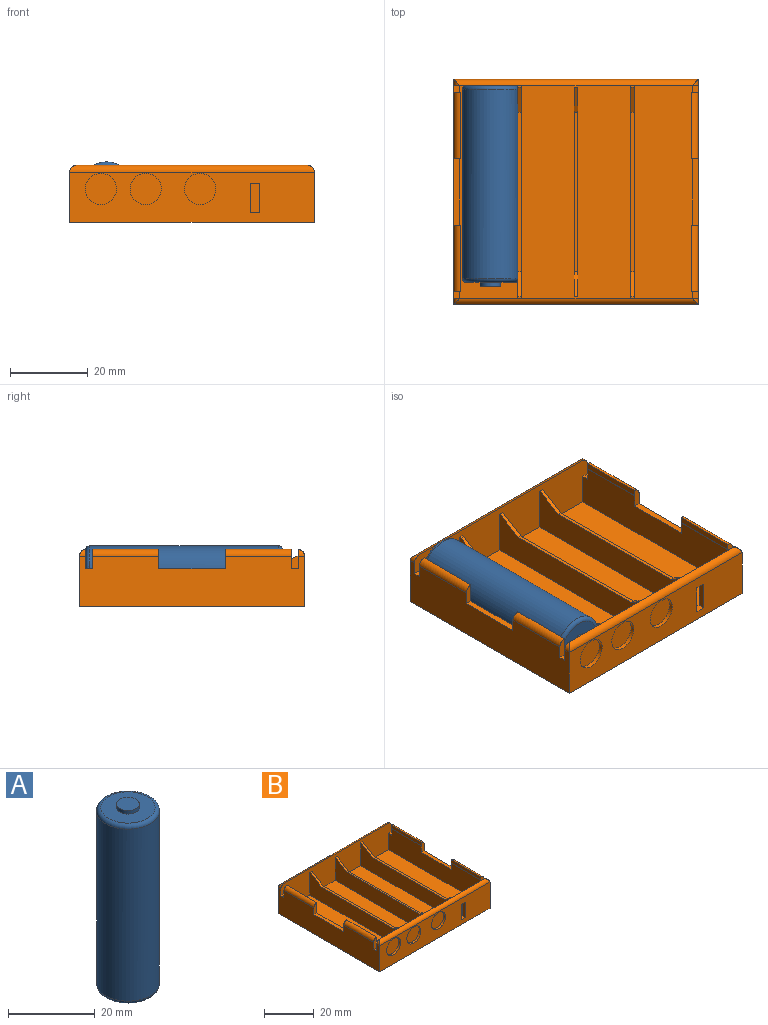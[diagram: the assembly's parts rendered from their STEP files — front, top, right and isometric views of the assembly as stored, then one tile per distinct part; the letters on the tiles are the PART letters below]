
ASSEMBLY  parts=2 mates=1
PART A: 7 faces, bbox 15.7x15.7x51.5 mm
  f0: plane 12.5x12.5mm, normal (0,0,-1), area 122.7mm2, adj f5
  f1: cylinder r=7.25mm len=48.5mm, axis (0,0,-1), area 2209.3mm2, adj f5,f6
  f2: plane 12.5x12.5mm, normal (0,0,1), area 101mm2, adj f3,f6
  f3: cylinder r=2.63mm len=5.26mm, axis (0,0,-1), area 16.5mm2, adj f2,f4
  f4: plane 5.26x5.26mm, normal (0,0,1), area 21.7mm2, adj f3
  f5: torus R=6.25mm, axis (0,0,1), area 68mm2, adj f0,f1
  f6: torus R=6.25mm, axis (0,0,-1), area 68mm2, adj f1,f2
PART B: 81 faces, bbox 62.8x57.8x14.6 mm
  f0: plane 54.6x14.8mm, normal (0,0,1), area 808.1mm2, adj f1,f4,f29,f74
  f1: plane 62.81x13.01mm, normal (0,-1,0), area 755.7mm2, adj f0,f2,f3,f7,f8,f12,f19,f24
  f2: plane 54.6x13.5mm, normal (0,0,1), area 737.1mm2, adj f1,f4,f68,f75
  f3: plane 54.6x13.5mm, normal (0,0,1), area 737.1mm2, adj f1,f4,f60,f67
  f4: plane 62.81x13.01mm, normal (0,1,0), area 737.7mm2, adj f0,f2,f3,f5,f6,f7,f10,f11
  f5: plane 2.4x1.6mm, normal (0,0,1), area 3.8mm2, adj f4,f21,f59,f61
  f6: plane 2.4x1.6mm, normal (0,0,-1), area 3.8mm2, adj f4,f21,f59,f61
  f7: plane 57.8x12.85mm, normal (-1,0,0), area 675.8mm2, adj f1,f4,f12,f13,f14,f20,f21,f22
  f8: cylinder r=1.75mm len=1.74mm, axis (0,-1,0), area 2.1mm2, adj f1,f19,f24
  f9: cylinder r=1.75mm len=17mm, axis (0,-1,0), area 46.7mm2, adj f15,f19,f41,f45
  f10: cylinder r=1.75mm len=1.74mm, axis (0,-1,0), area 2.1mm2, adj f4,f11,f19
  f11: cylinder r=1.75mm len=62.8mm, axis (-1,0,0), area 159.1mm2, adj f4,f10,f14,f21
  f12: cylinder r=1.75mm len=1.74mm, axis (0,1,0), area 2.1mm2, adj f1,f7,f24
  f13: cylinder r=1.75mm len=17mm, axis (0,1,0), area 46.7mm2, adj f7,f16,f37,f42
  f14: cylinder r=1.75mm len=1.74mm, axis (0,1,0), area 2.1mm2, adj f4,f7,f11
  f15: plane 17x1.6mm, normal (-1,0,0), area 27.2mm2, adj f9,f17,f41,f45
  f16: plane 17x1.6mm, normal (1,0,0), area 27.2mm2, adj f13,f18,f37,f42
  f17: cylinder r=0.15mm len=17mm, axis (0,-1,0), area 4mm2, adj f15,f28,f41,f45
  f18: cylinder r=0.15mm len=17mm, axis (0,1,0), area 4mm2, adj f16,f29,f37,f42
  f19: plane 57.8x12.85mm, normal (1,0,0), area 675.8mm2, adj f1,f4,f8,f9,f10,f20,f21,f22
  f20: plane 62.8x12.85mm, normal (0,1,0), area 676.8mm2, adj f7,f19,f22,f24,f47,f49,f51
  f21: plane 62.8x12.85mm, normal (0,-1,0), area 638.2mm2, adj f5,f6,f7,f11,f19,f22,f53,f54
  f22: plane 62.8x57.8mm, normal (0,0,-1), area 3629.8mm2, adj f7,f19,f20,f21
  f23: cylinder r=1.75mm len=17mm, axis (0,-1,0), area 46.7mm2, adj f19,f26,f34,f46
  f24: cylinder r=1.75mm len=62.8mm, axis (1,0,0), area 159.1mm2, adj f1,f8,f12,f20
  f25: cylinder r=1.75mm len=17mm, axis (0,1,0), area 46.7mm2, adj f7,f27,f35,f38
  f26: plane 17x1.6mm, normal (-1,0,0), area 27.2mm2, adj f23,f31,f34,f46
  f27: plane 17x1.6mm, normal (1,0,0), area 27.2mm2, adj f25,f32,f35,f38
  f28: plane 54.6x11.25mm, normal (-1,0,0), area 547.3mm2, adj f1,f4,f17,f30,f31,f33,f34,f40
  f29: plane 54.6x11.25mm, normal (1,0,0), area 547.3mm2, adj f0,f1,f4,f18,f32,f35,f36,f37
  f30: plane 54.6x14.8mm, normal (0,0,1), area 808.1mm2, adj f1,f4,f28,f61
  f31: cylinder r=0.15mm len=17mm, axis (0,-1,0), area 4mm2, adj f26,f28,f34,f46
  f32: cylinder r=0.15mm len=17mm, axis (0,1,0), area 4mm2, adj f27,f29,f35,f38
  f33: plane 1.8x1.6mm, normal (0,0,1), area 2.9mm2, adj f4,f19,f28,f34
  f34: plane 5x1.75mm, normal (0,-1,0), area 7.6mm2, adj f19,f23,f26,f28,f31,f33
  f35: plane 5x1.75mm, normal (0,-1,0), area 7.6mm2, adj f7,f25,f27,f29,f32,f36
  f36: plane 1.8x1.6mm, normal (0,0,1), area 2.9mm2, adj f4,f7,f29,f35
  f37: plane 5x1.75mm, normal (0,-1,0), area 7.6mm2, adj f7,f13,f16,f18,f29,f39
  f38: plane 5x1.75mm, normal (0,1,0), area 7.6mm2, adj f7,f25,f27,f29,f32,f39
  f39: plane 17x1.6mm, normal (0,0,1), area 27.2mm2, adj f7,f29,f37,f38
  f40: plane 1.8x1.6mm, normal (0,0,1), area 2.9mm2, adj f1,f19,f28,f41
  f41: plane 5x1.75mm, normal (0,1,0), area 7.6mm2, adj f9,f15,f17,f19,f28,f40
  f42: plane 5x1.75mm, normal (0,1,0), area 7.6mm2, adj f7,f13,f16,f18,f29,f43
  f43: plane 1.8x1.6mm, normal (0,0,1), area 2.9mm2, adj f1,f7,f29,f42
  f44: plane 17x1.6mm, normal (0,0,1), area 27.2mm2, adj f19,f28,f45,f46
  f45: plane 5x1.75mm, normal (0,-1,0), area 7.6mm2, adj f9,f15,f17,f19,f28,f44
  f46: plane 5x1.75mm, normal (0,1,0), area 7.6mm2, adj f19,f23,f26,f28,f31,f44
  f47: cylinder r=3.65mm len=7.3mm, axis (0,1,0), area 11.5mm2, adj f20,f48
  f48: plane 7.3x7.3mm, normal (0,1,0), area 41.9mm2, adj f47
  f49: cylinder r=3.75mm len=7.5mm, axis (0,1,0), area 11.8mm2, adj f20,f50
  f50: plane 7.5x7.5mm, normal (0,1,0), area 44.2mm2, adj f49
  f51: cylinder r=3.75mm len=7.5mm, axis (0,1,0), area 11.8mm2, adj f20,f52
  f52: plane 7.5x7.5mm, normal (0,1,0), area 44.2mm2, adj f51
  f53: cylinder r=4mm len=8mm, axis (0,-1,0), area 25.1mm2, adj f21,f58
  f54: cylinder r=4mm len=8mm, axis (0,-1,0), area 25.1mm2, adj f21,f57
  f55: cylinder r=4mm len=8mm, axis (0,-1,0), area 25.1mm2, adj f21,f56
  f56: plane 8x8mm, normal (0,-1,0), area 50.3mm2, adj f55
  f57: plane 8x8mm, normal (0,-1,0), area 50.3mm2, adj f54
  f58: plane 8x8mm, normal (0,-1,0), area 50.3mm2, adj f53
  f59: plane 7.5x1.6mm, normal (-1,0,0), area 12mm2, adj f4,f5,f6,f21
  f60: plane 54.6x11.25mm, normal (-1,0,0), area 426.7mm2, adj f1,f3,f4,f62,f63,f64,f65,f66
  f61: plane 56.2x11.25mm, normal (1,0,0), area 438.7mm2, adj f1,f4,f5,f6,f21,f30,f62,f63
  f62: plane 1x0.4mm, normal (0,0,1), area 0.4mm2, adj f1,f60,f61,f63
  f63: plane 6.37x3.95mm, normal (0,-0.53,0.85), area 7.5mm2, adj f60,f61,f62,f64
  f64: plane 41.05x1mm, normal (0,0,1), area 41.1mm2, adj f60,f61,f63,f65
  f65: plane 6.37x3.95mm, normal (0,0.53,0.85), area 7.5mm2, adj f60,f61,f64,f66
  f66: plane 1x0.4mm, normal (0,0,1), area 0.4mm2, adj f4,f60,f61,f65
  f67: plane 54.6x11.25mm, normal (1,0,0), area 426.7mm2, adj f1,f3,f4,f69,f70,f71,f72,f73
  f68: plane 54.6x11.25mm, normal (-1,0,0), area 426.7mm2, adj f1,f2,f4,f69,f70,f71,f72,f73
  f69: plane 1x0.4mm, normal (0,0,1), area 0.4mm2, adj f4,f67,f68,f70
  f70: plane 6.37x3.95mm, normal (0,0.53,0.85), area 7.5mm2, adj f67,f68,f69,f71
  f71: plane 41.05x1mm, normal (0,0,1), area 41.1mm2, adj f67,f68,f70,f72
  f72: plane 6.37x3.95mm, normal (0,-0.53,0.85), area 7.5mm2, adj f67,f68,f71,f73
  f73: plane 1x0.4mm, normal (0,0,1), area 0.4mm2, adj f1,f67,f68,f72
  f74: plane 54.6x11.25mm, normal (-1,0,0), area 426.7mm2, adj f0,f1,f4,f76,f77,f78,f79,f80
  f75: plane 54.6x11.25mm, normal (1,0,0), area 426.7mm2, adj f1,f2,f4,f76,f77,f78,f79,f80
  f76: plane 1x0.4mm, normal (0,0,1), area 0.4mm2, adj f1,f74,f75,f77
  f77: plane 6.37x3.95mm, normal (0,-0.53,0.85), area 7.5mm2, adj f74,f75,f76,f78
  f78: plane 41.05x1mm, normal (0,0,1), area 41.1mm2, adj f74,f75,f77,f79
  f79: plane 6.37x3.95mm, normal (0,0.53,0.85), area 7.5mm2, adj f74,f75,f78,f80
  f80: plane 1x0.4mm, normal (0,0,1), area 0.4mm2, adj f4,f74,f75,f79
PLACE A rot(axis=(0.58,0.58,-0.58),120deg) t=(-44.35,36.3,33.74)mm
PLACE B t=(-22.35,9,25.52)mm
MATE fastened A.f1 <-> B.f1  axis (0,1,0) through (-44.35,36.3,33.74)mm
